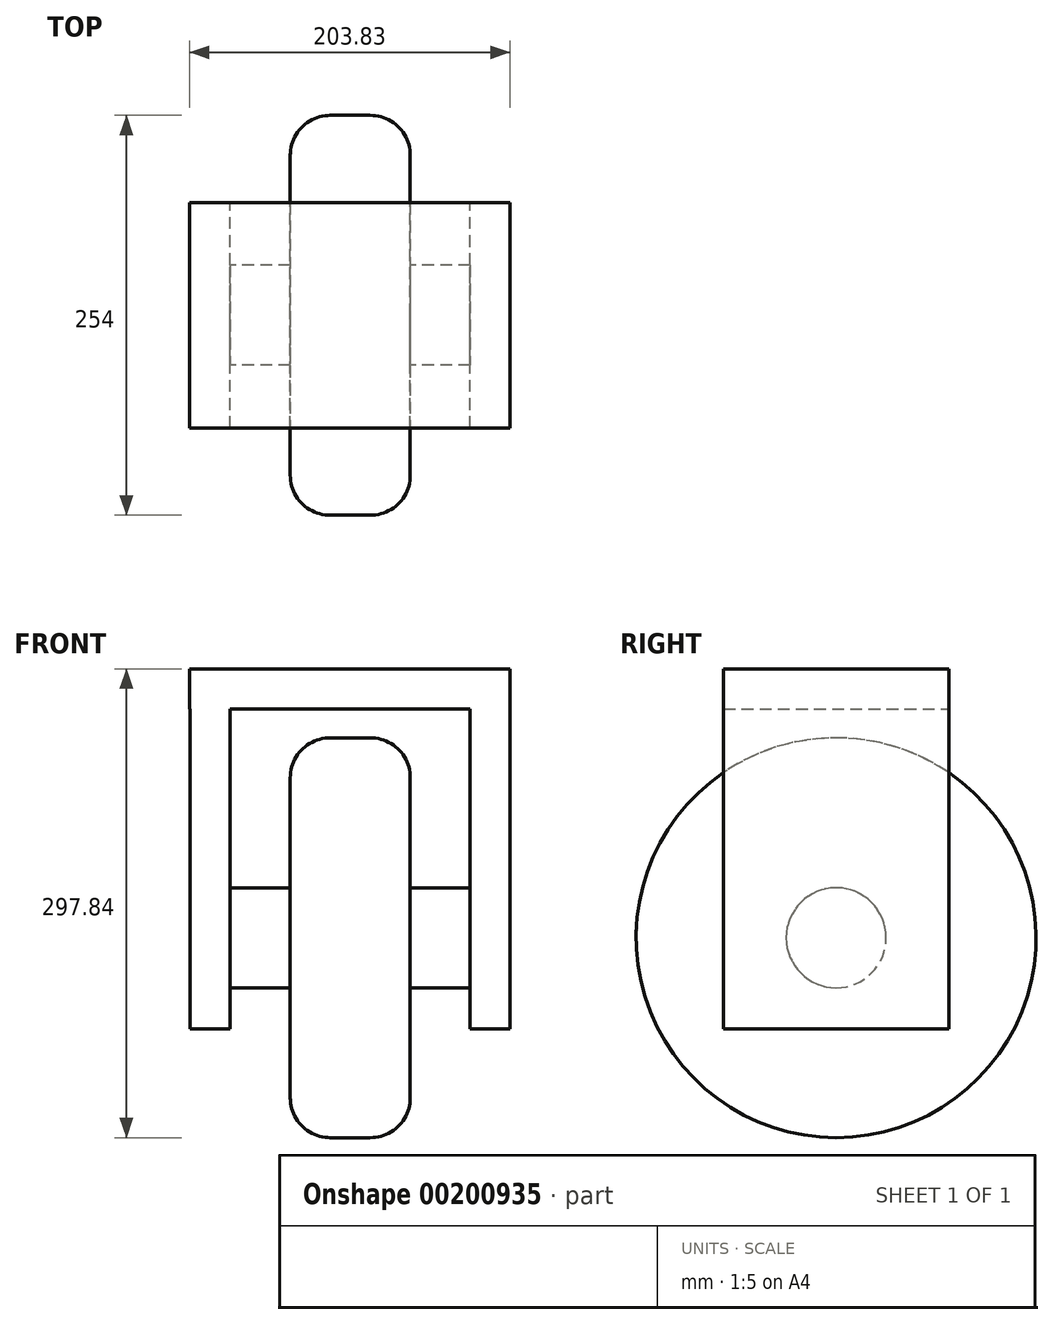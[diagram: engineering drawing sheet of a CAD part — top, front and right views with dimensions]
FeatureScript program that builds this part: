
annotation { "Feature Type Name" : "Feature", "Feature Type Description" : "" }
export const myFeature = defineFeature(function(context is Context, id is Id, definition is map)
    precondition{}
    {
        {
            var Q0;
            Q0=qCreatedBy(makeId("Right.planeOp"),FACE);
            var sketch = newSketch(context, id + "F0", { "sketchPlane" : qUnion([Q0])});
            skCircle(sketch, "E0", {"center": v(0, 0) * mm, "radius": 127 * mm});
            skPoint(sketch, "E1", {"position": v(-0.24, -0.49) * mm});
            skSolve(sketch);
        }
        {
            var Q0;
            Q0=makeQuery(id+"F0.imprint","IMPRINT",FACE,{"disambiguationData":[TD([[makeQuery(id+"F0.imprint","IMPRINT",EDGE,{"derivedFrom":sQuery(id+"F0.wireOp",EDGE,"E0")}),1.0]])]});
            extrude(context, id + "F1", {"entities" : qUnion([Q0]), "endBound" : BoundingType.SYMMETRIC, "depth" : 76.2 * mm});
        }
        {
            var Q0;
            Q0=qCreatedBy(makeId("Right.planeOp"),FACE);
            var sketch = newSketch(context, id + "F2", { "sketchPlane" : qUnion([Q0])});
            skCircle(sketch, "E2", {"center": v(0, 0) * mm, "radius": 31.75 * mm});
            skSolve(sketch);
        }
        {
            var Q0;
            Q0 = qSketchRegion(id + "F2", true);
            extrude(context, id + "F3", {"entities" : qUnion([Q0]), "operationType" : NewBodyOperationType.ADD, "endBound" : BoundingType.SYMMETRIC, "depth" : 203.2 * mm});
        }
        {
            var Q0;
            Q0=makeQuery(id+"F1.opExtrude","CAP_EDGE",EDGE,{"disambiguationData":[OSD([sQuery(id+"F0.wireOp",EDGE,"E0")])],"isStart":false});
            var Q1;
            Q1=makeQuery(id+"F1.opExtrude","CAP_EDGE",EDGE,{"disambiguationData":[OSD([sQuery(id+"F0.wireOp",EDGE,"E0")])],"isStart":true});
            fillet(context, id + "F4", {"entities" : qUnion([Q0, Q1]), "radius" : 25.4 * mm, "tangentPropagation" : true, "allowEdgeOverflow" : false});
        }
        {
            var Q0;
            Q0=sQuery(id+"F0.wireOp",VERTEX,"E1");
            var Q1;
            Q1=makeQuery(id+"F1.opExtrude","SWEPT_BODY",BODY,{"disambiguationData":[OSD([sQuery(id+"F0.wireOp",EDGE,"E0")])]});
            hole(context, id + "F5", {"style" : HoleStyle.SIMPLE, "endStyle" : HoleEndStyle.BLIND, "holeDiameter" : 76.2 * mm, "holeDepth" : 12.7 * mm, "startFromSketch" : true, "locations" : qUnion([Q0]), "scope" : qUnion([Q1])});
        }
        {
            var Q0;
            Q0=makeQuery(id+"F3.opExtrude","CAP_FACE",FACE,{"disambiguationData":[OSD([sQuery(id+"F2.wireOp",EDGE,"E2")])],"isStart":true});
            var sketch = newSketch(context, id + "F6", { "sketchPlane" : qUnion([Q0])});
            skLineSegment(sketch, "E3.top", {"start": v(0, -57.76) * mm, "end": v(71.53, -57.76) * mm});
            skLineSegment(sketch, "E3.left", {"start": v(0, -58.33) * mm, "end": v(0, -57.76) * mm});
            skLineSegment(sketch, "E3.right", {"start": v(71.53, -58.33) * mm, "end": v(71.53, -57.76) * mm});
            skLineSegment(sketch, "E4.top", {"start": v(71.53, 145.44) * mm, "end": v(-71.53, 145.44) * mm});
            skLineSegment(sketch, "E4.left", {"start": v(71.53, -57.76) * mm, "end": v(71.53, 145.44) * mm});
            skLineSegment(sketch, "E4.right", {"start": v(-71.53, -57.76) * mm, "end": v(-71.53, 145.44) * mm});
            skLineSegment(sketch, "E5", {"start": v(0, -57.76) * mm, "end": v(-71.53, -57.76) * mm});
            skPoint(sketch, "E6", {"position": v(0, 0) * mm});
            skPoint(sketch, "E7", {"position": v(-71.53, -57.76) * mm});
            skPoint(sketch, "E8", {"position": v(71.53, -57.76) * mm});
            skPoint(sketch, "E9", {"position": v(71.53, 145.44) * mm});
            skPoint(sketch, "E10", {"position": v(-71.53, 145.44) * mm});
            skSolve(sketch);
        }
        {
            var Q0;
            Q0=makeQuery(id+"F6.imprint","IMPRINT",FACE,{"disambiguationData":[TD([[makeQuery(id+"F6.imprint","IMPRINT",EDGE,{"derivedFrom":sQuery(id+"F6.wireOp",EDGE,"E3.top")}),1.0]])]});
            var Q1;
            Q1=sQuery(id+"F6.wireOp",EDGE,"E4.right");
            var Q2;
            Q2=makeQuery(id+"F1.opExtrude","CAP_FACE",FACE,{"disambiguationData":[OSD([sQuery(id+"F0.wireOp",EDGE,"E0")])],"isStart":true});
            extrude(context, id + "F7", {"entities" : qUnion([Q0]), "operationType" : NewBodyOperationType.ADD, "surfaceEntities" : qUnion([Q1]), "oppositeDirection" : true, "endBoundEntityFace" : qUnion([Q2]), "depth" : 25.4 * mm});
        }
        {
            var Q0;
            Q0=makeQuery(id+"F1.opExtrude","SWEPT_BODY",BODY,{"disambiguationData":[OSD([sQuery(id+"F0.wireOp",EDGE,"E0")])]});
            var Q1;
            Q1=qCreatedBy(makeId("Right.planeOp"),FACE);
            mirror(context, id + "F8", {"operationType" : NewBodyOperationType.ADD, "entities" : qUnion([Q0]), "mirrorPlane" : qUnion([Q1])});
        }
        {
            var Q0;
            Q0=makeQuery(id+"F8.opPattern","COPY",FACE,{"derivedFrom":makeQuery(id+"F7.opExtrude","SWEPT_FACE",FACE,{"disambiguationData":[OSD([sQuery(id+"F6.wireOp",EDGE,"E4.top")])]}),"instanceName":"1"});
            var sketch = newSketch(context, id + "F9", { "sketchPlane" : qUnion([Q0])});
            skLineSegment(sketch, "E11", {"start": v(101.6, 71.53) * mm, "end": v(-102.23, 71.53) * mm});
            skLineSegment(sketch, "E12", {"start": v(-102.23, 71.53) * mm, "end": v(-102.23, -71.53) * mm});
            skLineSegment(sketch, "E13", {"start": v(-102.23, -71.53) * mm, "end": v(101.6, -71.53) * mm});
            skLineSegment(sketch, "E14", {"start": v(101.6, -71.53) * mm, "end": v(101.6, 71.53) * mm});
            skLineSegment(sketch, "E15", {"start": v(76.2, 71.53) * mm, "end": v(101.6, 71.53) * mm});
            skLineSegment(sketch, "E16", {"start": v(76.2, -71.53) * mm, "end": v(101.6, -71.53) * mm});
            skLineSegment(sketch, "E17", {"start": v(101.6, 71.53) * mm, "end": v(101.6, -71.53) * mm});
            skSolve(sketch);
        }
        {
            var Q0;
            Q0 = qSketchRegion(id + "F9", true);
            extrude(context, id + "F10", {"entities" : qUnion([Q0]), "operationType" : NewBodyOperationType.ADD, "depth" : 25.4 * mm});
        }
    });
